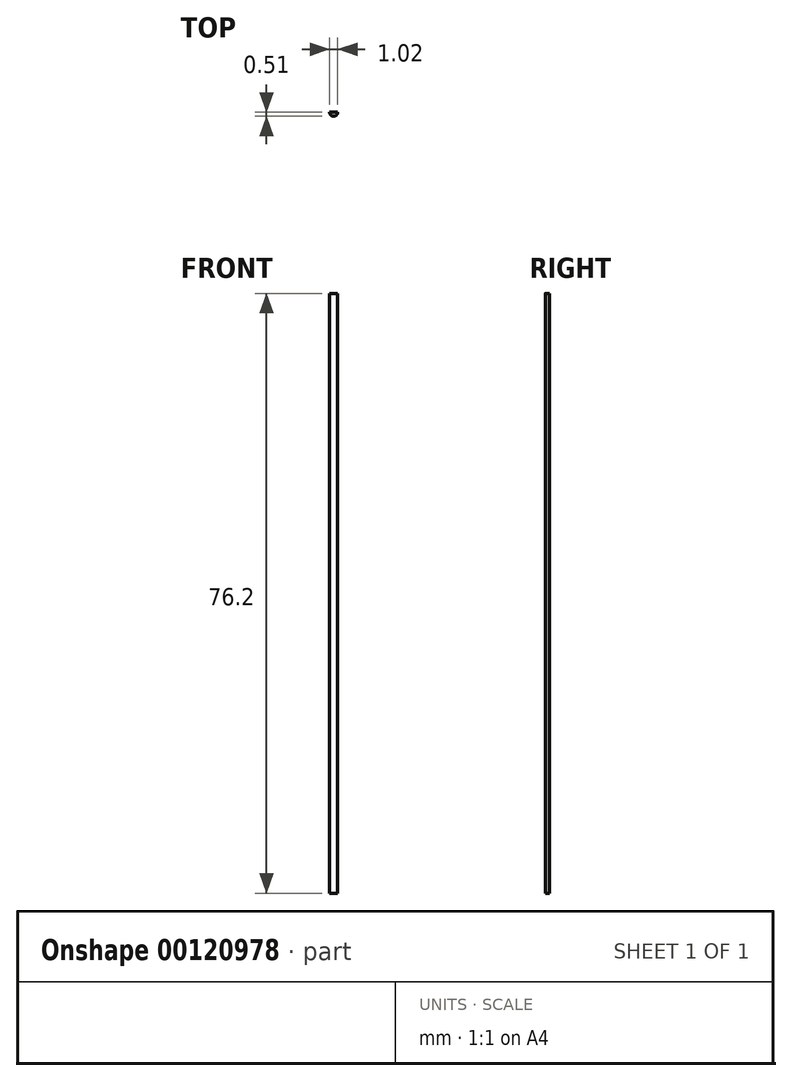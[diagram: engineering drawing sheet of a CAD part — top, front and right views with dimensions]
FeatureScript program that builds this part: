
annotation { "Feature Type Name" : "Feature", "Feature Type Description" : "" }
export const myFeature = defineFeature(function(context is Context, id is Id, definition is map)
    precondition{}
    {
        {
            var Q0;
            Q0=qCreatedBy(makeId("Front.planeOp"),FACE);
            var sketch = newSketch(context, id + "F0", { "sketchPlane" : qUnion([Q0])});
            skLineSegment(sketch, "E0.bottom", {"start": v(-45.79, 33.79) * mm, "end": v(-45.28, 33.79) * mm});
            skLineSegment(sketch, "E0.top", {"start": v(-45.79, -42.41) * mm, "end": v(-45.28, -42.41) * mm});
            skLineSegment(sketch, "E0.left", {"start": v(-45.79, 33.79) * mm, "end": v(-45.79, -42.41) * mm});
            skLineSegment(sketch, "E0.right", {"start": v(-45.28, 33.79) * mm, "end": v(-45.28, -42.41) * mm});
            skSolve(sketch);
        }
        {
            var Q0;
            Q0=makeQuery(id+"F0.imprint","IMPRINT",FACE,{"disambiguationData":[TD([[makeQuery(id+"F0.imprint","IMPRINT",EDGE,{"derivedFrom":sQuery(id+"F0.wireOp",EDGE,"E0.bottom")}),-1.0]])]});
            var Q1;
            Q1=sQuery(id+"F0.wireOp",EDGE,"E0.left");
            revolve(context, id + "F1", {"entities" : qUnion([Q0]), "axis" : qUnion([Q1]), "revolveType" : RevolveType.ONE_DIRECTION, "angle" : 180 * degree});
        }
    });
